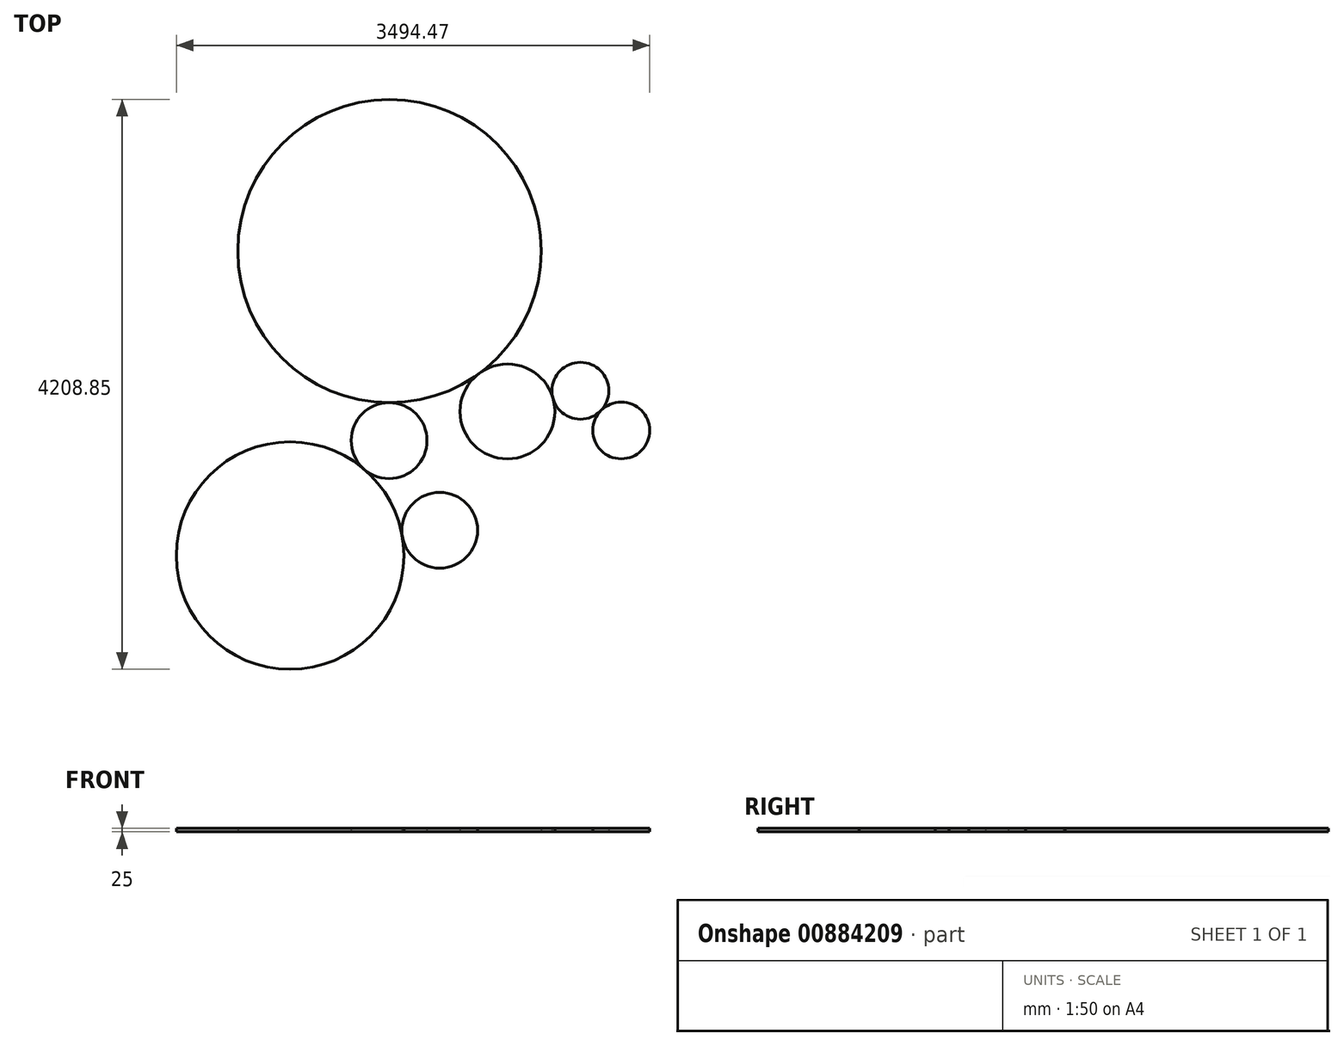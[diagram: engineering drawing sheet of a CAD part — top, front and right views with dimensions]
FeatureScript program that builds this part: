
annotation { "Feature Type Name" : "Feature", "Feature Type Description" : "" }
export const myFeature = defineFeature(function(context is Context, id is Id, definition is map)
    precondition{}
    {
        {
            var Q0;
            Q0=qCreatedBy(makeId("Top.planeOp"),FACE);
            var sketch = newSketch(context, id + "F0", { "sketchPlane" : qUnion([Q0])});
            skCircle(sketch, "E0", {"center": v(0, 210) * mm, "radius": 210 * mm});
            skLineSegment(sketch, "E1", {"start": v(0, 0) * mm, "end": v(765, 0) * mm, "construction": true});
            skLineSegment(sketch, "E2", {"start": v(0, 0) * mm, "end": v(-1060.2, 0) * mm, "construction": true});
            skCircle(sketch, "E3", {"center": v(-840, 350) * mm, "radius": 350 * mm});
            skCircle(sketch, "E4", {"center": v(-301.22, 502.7) * mm, "radius": 210 * mm});
            skLineSegment(sketch, "E5", {"start": v(-1060.2, 0) * mm, "end": v(-1060.2, -1292.3) * mm, "construction": true});
            skCircle(sketch, "E6", {"center": v(-1340.2, -527.3) * mm, "radius": 280 * mm});
            skCircle(sketch, "E7", {"center": v(-2444.47, -714.33) * mm, "radius": 840 * mm});
            skCircle(sketch, "E8", {"center": v(-1710.53, 1534.52) * mm, "radius": 1120 * mm});
            skCircle(sketch, "E9", {"center": v(-1713.82, 134.52) * mm, "radius": 280 * mm});
            skSolve(sketch);
        }
        {
            var Q0;
            Q0 = qSketchRegion(id + "F0", true);
            extrude(context, id + "F1", {"entities" : qUnion([Q0]), "depth" : 25 * mm, "offsetDistance" : 25 * mm});
        }
    });
